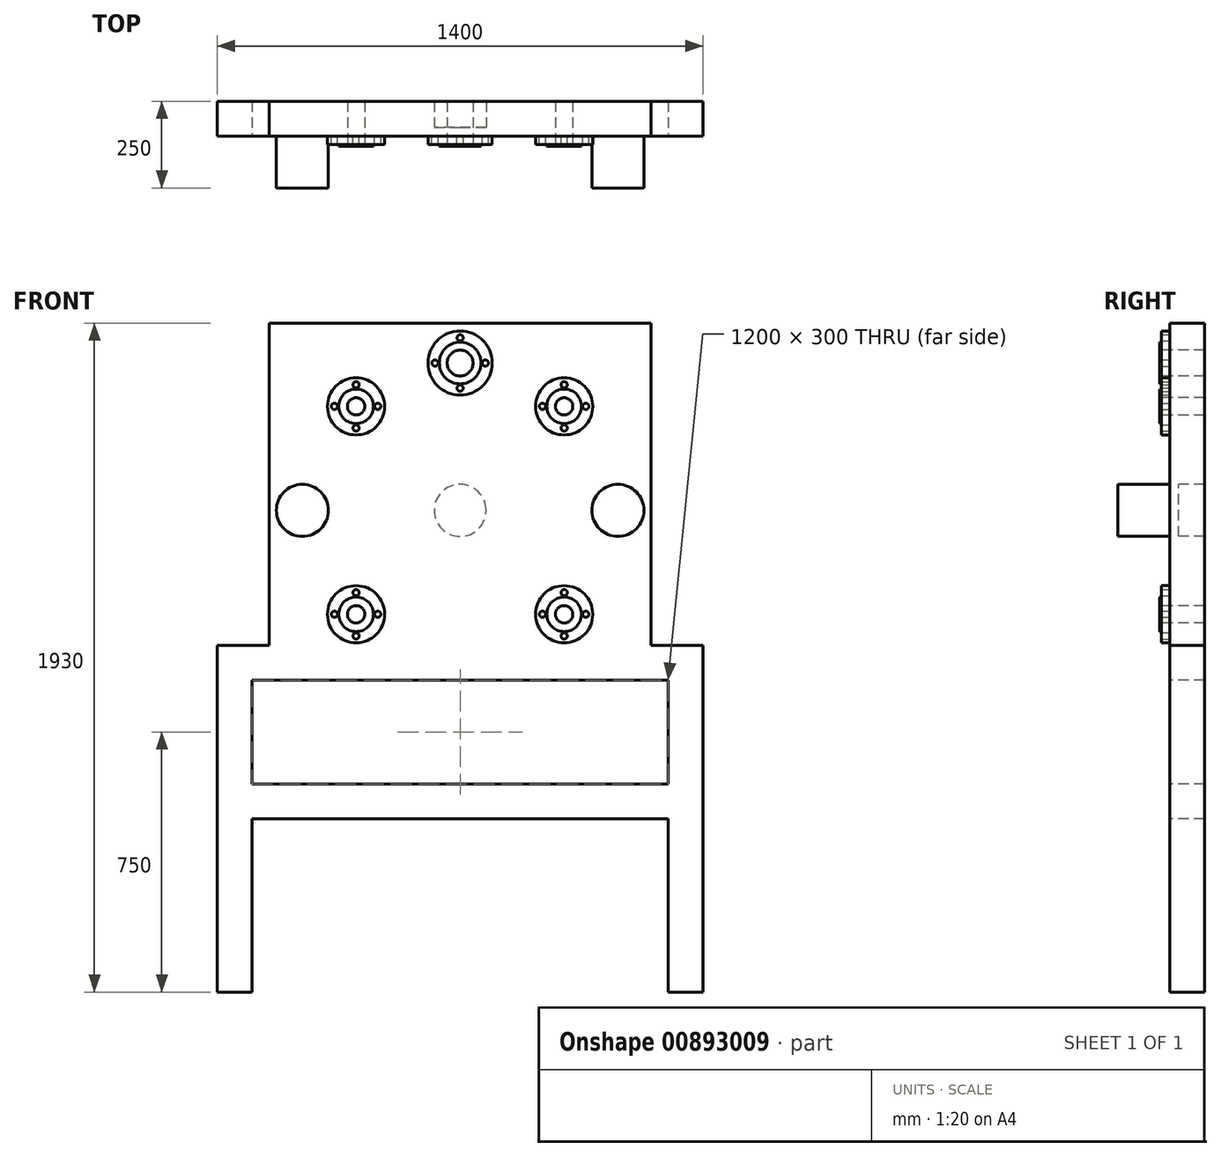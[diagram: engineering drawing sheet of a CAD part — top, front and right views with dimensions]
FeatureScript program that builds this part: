
annotation { "Feature Type Name" : "Feature", "Feature Type Description" : "" }
export const myFeature = defineFeature(function(context is Context, id is Id, definition is map)
    precondition{}
    {
        {
            var Q0;
            Q0=qCreatedBy(makeId("Front.planeOp"),FACE);
            var sketch = newSketch(context, id + "F0", { "sketchPlane" : qUnion([Q0])});
            skLineSegment(sketch, "E0.bottom", {"start": v(550, -965) * mm, "end": v(400, -965) * mm});
            skLineSegment(sketch, "E0.top", {"start": v(550, 965) * mm, "end": v(-550, 965) * mm});
            skLineSegment(sketch, "E0.left", {"start": v(550, -965) * mm, "end": v(550, 965) * mm});
            skLineSegment(sketch, "E0.right", {"start": v(-550, -965) * mm, "end": v(-550, 965) * mm});
            skPoint(sketch, "E0.middle", {"position": v(0, 0) * mm});
            skLineSegment(sketch, "E1.top", {"start": v(-400, -765) * mm, "end": v(400, -765) * mm});
            skLineSegment(sketch, "E1.left", {"start": v(-400, -965) * mm, "end": v(-400, -765) * mm});
            skLineSegment(sketch, "E1.right", {"start": v(400, -965) * mm, "end": v(400, -765) * mm});
            skLineSegment(sketch, "E2.bottom", {"start": v(-400, -615) * mm, "end": v(400, -615) * mm});
            skLineSegment(sketch, "E2.top", {"start": v(-400, -315) * mm, "end": v(400, -315) * mm});
            skLineSegment(sketch, "E2.left", {"start": v(-400, -615) * mm, "end": v(-400, -315) * mm});
            skLineSegment(sketch, "E2.right", {"start": v(400, -615) * mm, "end": v(400, -315) * mm});
            skLineSegment(sketch, "E3.trimOffspring", {"start": v(-400, -965) * mm, "end": v(-550, -965) * mm});
            skLineSegment(sketch, "E4.bottom", {"start": v(-400, -165) * mm, "end": v(400, -165) * mm});
            skLineSegment(sketch, "E4.top", {"start": v(-400, 35) * mm, "end": v(400, 35) * mm});
            skLineSegment(sketch, "E4.left", {"start": v(-400, -165) * mm, "end": v(-400, 35) * mm});
            skLineSegment(sketch, "E4.right", {"start": v(400, -165) * mm, "end": v(400, 35) * mm});
            skPoint(sketch, "E5.middle", {"position": v(0, 425) * mm});
            skSolve(sketch);
        }
        {
            var Q0;
            Q0=makeQuery(id+"F0.imprint","IMPRINT",FACE,{"disambiguationData":[TD([[makeQuery(id+"F0.imprint","IMPRINT",EDGE,{"derivedFrom":sQuery(id+"F0.wireOp",EDGE,"E0.bottom")}),-1.0]])]});
            extrude(context, id + "F1", {"entities" : qUnion([Q0]), "depth" : 100 * mm, "offsetDistance" : 25 * mm});
        }
        {
            var Q0;
            Q0=makeQuery(id+"F1.opExtrude","CAP_FACE",FACE,{"disambiguationData":[OSD([sQuery(id+"F0.wireOp",EDGE,"E0.bottom"),sQuery(id+"F0.wireOp",EDGE,"E0.top"),sQuery(id+"F0.wireOp",EDGE,"E0.left"),sQuery(id+"F0.wireOp",EDGE,"E0.right"),sQuery(id+"F0.wireOp",EDGE,"E1.top"),sQuery(id+"F0.wireOp",EDGE,"E1.left"),sQuery(id+"F0.wireOp",EDGE,"E1.right"),sQuery(id+"F0.wireOp",EDGE,"E2.bottom"),sQuery(id+"F0.wireOp",EDGE,"E2.top"),sQuery(id+"F0.wireOp",EDGE,"E2.left"),sQuery(id+"F0.wireOp",EDGE,"E2.right"),sQuery(id+"F0.wireOp",EDGE,"E3.trimOffspring"),sQuery(id+"F0.wireOp",EDGE,"nSGubIzk-R7de-6MO4-penA-cvBglKJnvsGC"),sQuery(id+"F0.wireOp",EDGE,"E4.bottom"),sQuery(id+"F0.wireOp",EDGE,"E4.top"),sQuery(id+"F0.wireOp",EDGE,"E4.left"),sQuery(id+"F0.wireOp",EDGE,"E4.right")])],"isStart":false});
            var sketch = newSketch(context, id + "F2", { "sketchPlane" : qUnion([Q0])});
            skCircle(sketch, "E6", {"center": v(-300, 125) * mm, "radius": 25 * mm});
            skCircle(sketch, "E7.0", {"center": v(0, 425) * mm, "radius": 75 * mm});
            skCircle(sketch, "E8.0.1.0", {"center": v(-300, 725) * mm, "radius": 25 * mm});
            skCircle(sketch, "E8.1.0.0", {"center": v(300, 125) * mm, "radius": 25 * mm});
            skCircle(sketch, "E8.1.1.0", {"center": v(300, 725) * mm, "radius": 25 * mm});
            skLineSegment(sketch, "E8.direction1", {"start": v(-300, 125) * mm, "end": v(300, 125) * mm, "construction": true});
            skLineSegment(sketch, "E8.direction2", {"start": v(-300, 125) * mm, "end": v(-300, 725) * mm, "construction": true});
            skSolve(sketch);
        }
        {
            var Q0;
            Q0=qSketchRegion(id+"F2",true);
            extrude(context, id + "F3", {"entities" : qUnion([Q0]), "operationType" : NewBodyOperationType.REMOVE, "oppositeDirection" : true, "depth" : 100 * mm, "offsetDistance" : 25 * mm});
        }
        {
            var Q0;
            Q0=makeQuery(id+"F1.opExtrude","CAP_FACE",FACE,{"disambiguationData":[OSD([sQuery(id+"F0.wireOp",EDGE,"E0.bottom"),sQuery(id+"F0.wireOp",EDGE,"E0.top"),sQuery(id+"F0.wireOp",EDGE,"E0.left"),sQuery(id+"F0.wireOp",EDGE,"E0.right"),sQuery(id+"F0.wireOp",EDGE,"E1.top"),sQuery(id+"F0.wireOp",EDGE,"E1.left"),sQuery(id+"F0.wireOp",EDGE,"E1.right"),sQuery(id+"F0.wireOp",EDGE,"E2.bottom"),sQuery(id+"F0.wireOp",EDGE,"E2.top"),sQuery(id+"F0.wireOp",EDGE,"E2.left"),sQuery(id+"F0.wireOp",EDGE,"E2.right"),sQuery(id+"F0.wireOp",EDGE,"E3.trimOffspring"),sQuery(id+"F0.wireOp",EDGE,"nSGubIzk-R7de-6MO4-penA-cvBglKJnvsGC"),sQuery(id+"F0.wireOp",EDGE,"E4.bottom"),sQuery(id+"F0.wireOp",EDGE,"E4.top"),sQuery(id+"F0.wireOp",EDGE,"E4.left"),sQuery(id+"F0.wireOp",EDGE,"E4.right")])],"isStart":false});
            var sketch = newSketch(context, id + "F4", { "sketchPlane" : qUnion([Q0])});
            skCircle(sketch, "E9", {"center": v(-455, 425) * mm, "radius": 75 * mm});
            skCircle(sketch, "E10.MirrorC", {"center": v(455, 425) * mm, "radius": 75 * mm});
            skSolve(sketch);
        }
        {
            var Q0;
            Q0=qSketchRegion(id+"F4",true);
            extrude(context, id + "F5", {"entities" : qUnion([Q0]), "operationType" : NewBodyOperationType.ADD, "depth" : 150 * mm, "offsetDistance" : 25 * mm});
        }
        {
            var Q0;
            Q0=makeQuery(id+"F1.opExtrude","CAP_FACE",FACE,{"disambiguationData":[OSD([sQuery(id+"F0.wireOp",EDGE,"E0.bottom"),sQuery(id+"F0.wireOp",EDGE,"E0.top"),sQuery(id+"F0.wireOp",EDGE,"E0.left"),sQuery(id+"F0.wireOp",EDGE,"E0.right"),sQuery(id+"F0.wireOp",EDGE,"E1.top"),sQuery(id+"F0.wireOp",EDGE,"E1.left"),sQuery(id+"F0.wireOp",EDGE,"E1.right"),sQuery(id+"F0.wireOp",EDGE,"E2.bottom"),sQuery(id+"F0.wireOp",EDGE,"E2.top"),sQuery(id+"F0.wireOp",EDGE,"E2.left"),sQuery(id+"F0.wireOp",EDGE,"E2.right"),sQuery(id+"F0.wireOp",EDGE,"E3.trimOffspring"),sQuery(id+"F0.wireOp",EDGE,"nSGubIzk-R7de-6MO4-penA-cvBglKJnvsGC"),sQuery(id+"F0.wireOp",EDGE,"E4.bottom"),sQuery(id+"F0.wireOp",EDGE,"E4.top"),sQuery(id+"F0.wireOp",EDGE,"E4.left"),sQuery(id+"F0.wireOp",EDGE,"E4.right")])],"isStart":false});
            var sketch = newSketch(context, id + "F6", { "sketchPlane" : qUnion([Q0])});
            skCircle(sketch, "E11", {"center": v(-300, 725) * mm, "radius": 82.5 * mm});
            skCircle(sketch, "E12", {"center": v(-300, 787.5) * mm, "radius": 9 * mm});
            skCircle(sketch, "E13.0", {"center": v(-300, 725) * mm, "radius": 25 * mm});
            skCircle(sketch, "E14.1.0", {"center": v(-362.5, 725) * mm, "radius": 9 * mm});
            skCircle(sketch, "E14.2.0", {"center": v(-300, 662.5) * mm, "radius": 9 * mm});
            skCircle(sketch, "E14.3.0", {"center": v(-237.5, 725) * mm, "radius": 9 * mm});
            skPoint(sketch, "E15.0.1.0", {"position": v(-300, 125) * mm});
            skCircle(sketch, "E15.0.1.1", {"center": v(-300, 125) * mm, "radius": 82.5 * mm});
            skCircle(sketch, "E15.0.1.2", {"center": v(-300, 125) * mm, "radius": 25 * mm});
            skCircle(sketch, "E15.0.1.3", {"center": v(-237.5, 125) * mm, "radius": 9 * mm});
            skCircle(sketch, "E15.0.1.4", {"center": v(-362.5, 125) * mm, "radius": 9 * mm});
            skCircle(sketch, "E15.0.1.5", {"center": v(-300, 187.5) * mm, "radius": 9 * mm});
            skCircle(sketch, "E15.0.1.6", {"center": v(-300, 62.5) * mm, "radius": 9 * mm});
            skPoint(sketch, "E15.1.0.0", {"position": v(300, 725) * mm});
            skCircle(sketch, "E15.1.0.1", {"center": v(300, 725) * mm, "radius": 82.5 * mm});
            skCircle(sketch, "E15.1.0.2", {"center": v(300, 725) * mm, "radius": 25 * mm});
            skCircle(sketch, "E15.1.0.3", {"center": v(362.5, 725) * mm, "radius": 9 * mm});
            skCircle(sketch, "E15.1.0.4", {"center": v(237.5, 725) * mm, "radius": 9 * mm});
            skCircle(sketch, "E15.1.0.5", {"center": v(300, 787.5) * mm, "radius": 9 * mm});
            skCircle(sketch, "E15.1.0.6", {"center": v(300, 662.5) * mm, "radius": 9 * mm});
            skPoint(sketch, "E15.1.1.0", {"position": v(300, 125) * mm});
            skCircle(sketch, "E15.1.1.1", {"center": v(300, 125) * mm, "radius": 82.5 * mm});
            skCircle(sketch, "E15.1.1.2", {"center": v(300, 125) * mm, "radius": 25 * mm});
            skCircle(sketch, "E15.1.1.3", {"center": v(362.5, 125) * mm, "radius": 9 * mm});
            skCircle(sketch, "E15.1.1.4", {"center": v(237.5, 125) * mm, "radius": 9 * mm});
            skCircle(sketch, "E15.1.1.5", {"center": v(300, 187.5) * mm, "radius": 9 * mm});
            skCircle(sketch, "E15.1.1.6", {"center": v(300, 62.5) * mm, "radius": 9 * mm});
            skLineSegment(sketch, "E15.direction1", {"start": v(-300, 662.5) * mm, "end": v(300, 662.5) * mm, "construction": true});
            skLineSegment(sketch, "E15.direction2", {"start": v(-300, 662.5) * mm, "end": v(-300, 62.5) * mm, "construction": true});
            skSolve(sketch);
        }
        {
            var Q0;
            Q0=qSketchRegion(id+"F6",true);
            extrude(context, id + "F7", {"entities" : qUnion([Q0]), "operationType" : NewBodyOperationType.ADD, "depth" : 25 * mm, "offsetDistance" : 25 * mm});
        }
        {
            var Q0;
            Q0=makeQuery(id+"F7.opExtrude","CAP_FACE",FACE,{"disambiguationData":[OSD([sQuery(id+"F6.wireOp",EDGE,"E11"),sQuery(id+"F6.wireOp",EDGE,"E12"),sQuery(id+"F6.wireOp",EDGE,"E13.0"),sQuery(id+"F6.wireOp",EDGE,"E14.1.0"),sQuery(id+"F6.wireOp",EDGE,"E14.2.0"),sQuery(id+"F6.wireOp",EDGE,"E14.3.0")])],"isStart":false});
            var sketch = newSketch(context, id + "F8", { "sketchPlane" : qUnion([Q0])});
            skCircle(sketch, "E16", {"center": v(-300, 725) * mm, "radius": 50 * mm});
            skCircle(sketch, "E17.0.1.0", {"center": v(-300, 125) * mm, "radius": 50 * mm});
            skCircle(sketch, "E17.1.0.0", {"center": v(300, 725) * mm, "radius": 50 * mm});
            skCircle(sketch, "E17.1.1.0", {"center": v(300, 125) * mm, "radius": 50 * mm});
            skLineSegment(sketch, "E17.direction1", {"start": v(-300, 725) * mm, "end": v(300, 725) * mm, "construction": true});
            skLineSegment(sketch, "E17.direction2", {"start": v(-300, 725) * mm, "end": v(-300, 125) * mm, "construction": true});
            skCircle(sketch, "E18", {"center": v(300, 725) * mm, "radius": 25 * mm});
            skCircle(sketch, "E19", {"center": v(300, 125) * mm, "radius": 25 * mm});
            skCircle(sketch, "E20", {"center": v(-300, 125) * mm, "radius": 25 * mm});
            skCircle(sketch, "E21", {"center": v(-300, 725) * mm, "radius": 25 * mm});
            skSolve(sketch);
        }
        {
            var Q0;
            Q0=qSketchRegion(id+"F8",true);
            extrude(context, id + "F9", {"entities" : qUnion([Q0]), "operationType" : NewBodyOperationType.ADD, "depth" : 5 * mm, "offsetDistance" : 25 * mm});
        }
        {
            var Q0;
            {var subQ0=sQuery(id+"F0.wireOp",EDGE,"E4.right");var subQ1=sQuery(id+"F0.wireOp",EDGE,"E4.left");var subQ2=sQuery(id+"F0.wireOp",EDGE,"E4.top");var subQ3=sQuery(id+"F0.wireOp",EDGE,"E1.left");var subQ4=sQuery(id+"F0.wireOp",EDGE,"E4.bottom");var subQ5=sQuery(id+"F0.wireOp",EDGE,"E3.trimOffspring");var subQ6=sQuery(id+"F0.wireOp",EDGE,"E2.right");var subQ7=sQuery(id+"F0.wireOp",EDGE,"E0.left");var subQ8=sQuery(id+"F0.wireOp",EDGE,"E0.top");var subQ9=sQuery(id+"F0.wireOp",EDGE,"E0.right");var subQ10=sQuery(id+"F0.wireOp",EDGE,"E2.bottom");var subQ11=sQuery(id+"F0.wireOp",EDGE,"E0.bottom");var subQ12=sQuery(id+"F0.wireOp",EDGE,"E2.left");var subQ13=sQuery(id+"F0.wireOp",EDGE,"E1.top");var subQ14=sQuery(id+"F0.wireOp",EDGE,"E1.right");var subQ15=sQuery(id+"F0.wireOp",EDGE,"E2.top");Q0=makeQuery(id+"F7.boolean.opBoolean","SPLIT",FACE,{"disambiguationData":[TD([makeQuery(id+"F1.opExtrude","SWEPT_FACE",FACE,{"disambiguationData":[OSD([subQ11])]})])],"derivedFrom":makeQuery(id+"F1.opExtrude","CAP_FACE",FACE,{"disambiguationData":[OSD([subQ11,subQ8,subQ7,subQ9,subQ13,subQ3,subQ14,subQ10,subQ15,subQ12,subQ6,subQ5,subQ4,subQ2,subQ1,subQ0])],"isStart":false})});}
            var sketch = newSketch(context, id + "F10", { "sketchPlane" : qUnion([Q0])});
            skCircle(sketch, "E22.0", {"center": v(0, 425) * mm, "radius": 75 * mm});
            skSolve(sketch);
        }
        {
            var Q0;
            Q0=qSketchRegion(id+"F10",true);
            extrude(context, id + "F11", {"entities" : qUnion([Q0]), "operationType" : NewBodyOperationType.ADD, "oppositeDirection" : true, "depth" : 25 * mm, "offsetDistance" : 25 * mm});
        }
        {
            var Q0;
            {var subQ0=sQuery(id+"F0.wireOp",EDGE,"E4.right");var subQ1=sQuery(id+"F0.wireOp",EDGE,"E4.left");var subQ2=sQuery(id+"F0.wireOp",EDGE,"E4.top");var subQ3=sQuery(id+"F0.wireOp",EDGE,"E1.left");var subQ4=sQuery(id+"F0.wireOp",EDGE,"E4.bottom");var subQ5=sQuery(id+"F0.wireOp",EDGE,"E3.trimOffspring");var subQ6=sQuery(id+"F0.wireOp",EDGE,"E2.right");var subQ7=sQuery(id+"F0.wireOp",EDGE,"E0.left");var subQ8=sQuery(id+"F0.wireOp",EDGE,"E0.top");var subQ9=sQuery(id+"F0.wireOp",EDGE,"E0.right");var subQ10=sQuery(id+"F0.wireOp",EDGE,"E2.bottom");var subQ11=sQuery(id+"F0.wireOp",EDGE,"E0.bottom");var subQ12=sQuery(id+"F0.wireOp",EDGE,"E2.left");var subQ13=sQuery(id+"F0.wireOp",EDGE,"E1.top");var subQ14=sQuery(id+"F0.wireOp",EDGE,"E1.right");var subQ15=sQuery(id+"F0.wireOp",EDGE,"E2.top");Q0=makeQuery(id+"F11.boolean.opBoolean","MERGE",FACE,{"derivedFrom":[makeQuery(id+"F7.boolean.opBoolean","SPLIT",FACE,{"disambiguationData":[TD([makeQuery(id+"F1.opExtrude","SWEPT_FACE",FACE,{"disambiguationData":[OSD([subQ11])]})])],"derivedFrom":makeQuery(id+"F1.opExtrude","CAP_FACE",FACE,{"disambiguationData":[OSD([subQ11,subQ8,subQ7,subQ9,subQ13,subQ3,subQ14,subQ10,subQ15,subQ12,subQ6,subQ5,subQ4,subQ2,subQ1,subQ0])],"isStart":false})}),makeQuery(id+"F11.opExtrude","CAP_FACE",FACE,{"disambiguationData":[OSD([sQuery(id+"F10.wireOp",EDGE,"E22.0")])],"isStart":true})]});}
            var sketch = newSketch(context, id + "F12", { "sketchPlane" : qUnion([Q0])});
            skCircle(sketch, "E23", {"center": v(0, 850) * mm, "radius": 37.5 * mm});
            skPoint(sketch, "E23.centerSnap0", {"position": v(0, 965) * mm});
            skCircle(sketch, "E24.0", {"center": v(300, 725) * mm, "radius": 25 * mm});
            skSolve(sketch);
        }
        {
            var Q0;
            Q0=makeQuery(id+"F12.imprint","IMPRINT",FACE,{"disambiguationData":[TD([[makeQuery(id+"F12.imprint","IMPRINT",EDGE,{"derivedFrom":sQuery(id+"F12.wireOp",EDGE,"E23")}),1.0]])]});
            extrude(context, id + "F13", {"entities" : qUnion([Q0]), "operationType" : NewBodyOperationType.REMOVE, "oppositeDirection" : true, "depth" : 100 * mm, "offsetDistance" : 25 * mm});
        }
        {
            var Q0;
            {var subQ0=sQuery(id+"F0.wireOp",EDGE,"E4.right");var subQ1=sQuery(id+"F0.wireOp",EDGE,"E4.left");var subQ2=sQuery(id+"F0.wireOp",EDGE,"E4.top");var subQ3=sQuery(id+"F0.wireOp",EDGE,"E1.left");var subQ4=sQuery(id+"F0.wireOp",EDGE,"E4.bottom");var subQ5=sQuery(id+"F0.wireOp",EDGE,"E3.trimOffspring");var subQ6=sQuery(id+"F0.wireOp",EDGE,"E2.right");var subQ7=sQuery(id+"F0.wireOp",EDGE,"E0.left");var subQ8=sQuery(id+"F0.wireOp",EDGE,"E0.top");var subQ9=sQuery(id+"F0.wireOp",EDGE,"E0.right");var subQ10=sQuery(id+"F0.wireOp",EDGE,"E2.bottom");var subQ11=sQuery(id+"F0.wireOp",EDGE,"E0.bottom");var subQ12=sQuery(id+"F0.wireOp",EDGE,"E2.left");var subQ13=sQuery(id+"F0.wireOp",EDGE,"E1.top");var subQ14=sQuery(id+"F0.wireOp",EDGE,"E1.right");var subQ15=sQuery(id+"F0.wireOp",EDGE,"E2.top");Q0=makeQuery(id+"F11.boolean.opBoolean","MERGE",FACE,{"derivedFrom":[makeQuery(id+"F7.boolean.opBoolean","SPLIT",FACE,{"disambiguationData":[TD([makeQuery(id+"F1.opExtrude","SWEPT_FACE",FACE,{"disambiguationData":[OSD([subQ11])]})])],"derivedFrom":makeQuery(id+"F1.opExtrude","CAP_FACE",FACE,{"disambiguationData":[OSD([subQ11,subQ8,subQ7,subQ9,subQ13,subQ3,subQ14,subQ10,subQ15,subQ12,subQ6,subQ5,subQ4,subQ2,subQ1,subQ0])],"isStart":false})}),makeQuery(id+"F11.opExtrude","CAP_FACE",FACE,{"disambiguationData":[OSD([sQuery(id+"F10.wireOp",EDGE,"E22.0")])],"isStart":true})]});}
            var sketch = newSketch(context, id + "F14", { "sketchPlane" : qUnion([Q0])});
            skCircle(sketch, "E25", {"center": v(0, 850) * mm, "radius": 92.5 * mm});
            skCircle(sketch, "E26", {"center": v(0, 922.5) * mm, "radius": 9 * mm});
            skCircle(sketch, "E27.1.0", {"center": v(-72.5, 850) * mm, "radius": 9 * mm});
            skCircle(sketch, "E27.2.0", {"center": v(0, 777.5) * mm, "radius": 9 * mm});
            skCircle(sketch, "E27.3.0", {"center": v(72.5, 850) * mm, "radius": 9 * mm});
            skSolve(sketch);
        }
        {
            var Q0;
            Q0=makeQuery(id+"F14.imprint","IMPRINT",FACE,{"disambiguationData":[TD([[makeQuery(id+"F14.imprint","IMPRINT",EDGE,{"derivedFrom":sQuery(id+"F14.wireOp",EDGE,"E25")}),1.0]])]});
            extrude(context, id + "F15", {"entities" : qUnion([Q0]), "operationType" : NewBodyOperationType.ADD, "depth" : 25 * mm, "offsetDistance" : 25 * mm});
        }
        {
            var Q0;
            Q0=makeQuery(id+"F15.opExtrude","CAP_FACE",FACE,{"disambiguationData":[OSD([sQuery(id+"F12.wireOp",EDGE,"E23"),sQuery(id+"F14.wireOp",EDGE,"E25"),sQuery(id+"F14.wireOp",EDGE,"E26"),sQuery(id+"F14.wireOp",EDGE,"E27.1.0"),sQuery(id+"F14.wireOp",EDGE,"E27.2.0"),sQuery(id+"F14.wireOp",EDGE,"E27.3.0")])],"isStart":false});
            var sketch = newSketch(context, id + "F16", { "sketchPlane" : qUnion([Q0])});
            skCircle(sketch, "E28", {"center": v(0, 850) * mm, "radius": 60 * mm});
            skSolve(sketch);
        }
        {
            var Q0;
            Q0=makeQuery(id+"F16.imprint","IMPRINT",FACE,{"disambiguationData":[TD([[makeQuery(id+"F16.imprint","IMPRINT",EDGE,{"derivedFrom":sQuery(id+"F16.wireOp",EDGE,"E28")}),1.0]])]});
            extrude(context, id + "F17", {"entities" : qUnion([Q0]), "operationType" : NewBodyOperationType.ADD, "depth" : 5 * mm, "offsetDistance" : 25 * mm});
        }
        {
            var Q0;
            {var subQ2=sQuery(id+"F0.wireOp",EDGE,"E4.right");var subQ5=sQuery(id+"F0.wireOp",EDGE,"E4.left");var subQ8=sQuery(id+"F0.wireOp",EDGE,"E4.top");var subQ10=sQuery(id+"F0.wireOp",EDGE,"E4.bottom");var subQ12=sQuery(id+"F0.wireOp",EDGE,"E3.trimOffspring");var subQ14=sQuery(id+"F0.wireOp",EDGE,"E2.right");var subQ16=sQuery(id+"F0.wireOp",EDGE,"E0.left");var subQ18=sQuery(id+"F0.wireOp",EDGE,"E0.top");var subQ20=sQuery(id+"F0.wireOp",EDGE,"E0.right");var subQ23=sQuery(id+"F0.wireOp",EDGE,"E2.bottom");var subQ25=sQuery(id+"F0.wireOp",EDGE,"E0.bottom");var subQ26=makeQuery(id+"F1.opExtrude","SWEPT_FACE",FACE,{"disambiguationData":[OSD([subQ25])]});var subQ27=sQuery(id+"F0.wireOp",EDGE,"E2.left");var subQ29=sQuery(id+"F0.wireOp",EDGE,"E1.top");var subQ32=sQuery(id+"F0.wireOp",EDGE,"E1.left");var subQ34=sQuery(id+"F0.wireOp",EDGE,"E1.right");var subQ36=sQuery(id+"F0.wireOp",EDGE,"E2.top");Q0=makeQuery(id+"F15.boolean.opBoolean","SPLIT",FACE,{"disambiguationData":[TD([subQ26])],"derivedFrom":makeQuery(id+"F11.boolean.opBoolean","MERGE",FACE,{"derivedFrom":[makeQuery(id+"F7.boolean.opBoolean","SPLIT",FACE,{"disambiguationData":[TD([subQ26])],"derivedFrom":makeQuery(id+"F1.opExtrude","CAP_FACE",FACE,{"disambiguationData":[OSD([subQ25,subQ18,subQ16,subQ20,subQ29,subQ32,subQ34,subQ23,subQ36,subQ27,subQ14,subQ12,subQ10,subQ8,subQ5,subQ2])],"isStart":false})}),makeQuery(id+"F11.opExtrude","CAP_FACE",FACE,{"disambiguationData":[OSD([sQuery(id+"F10.wireOp",EDGE,"E22.0")])],"isStart":true})]})});}
            var sketch = newSketch(context, id + "F18", { "sketchPlane" : qUnion([Q0])});
            skLineSegment(sketch, "E29.bottom", {"start": v(-568.84, 35) * mm, "end": v(631.16, 35) * mm});
            skLineSegment(sketch, "E29.top", {"start": v(-568.84, -965) * mm, "end": v(631.16, -965) * mm});
            skLineSegment(sketch, "E29.left", {"start": v(-568.84, 35) * mm, "end": v(-568.84, -965) * mm});
            skLineSegment(sketch, "E29.right", {"start": v(631.16, 35) * mm, "end": v(631.16, -965) * mm});
            skSolve(sketch);
        }
        {
            var Q0;
            Q0=qSketchRegion(id+"F18",true);
            extrude(context, id + "F19", {"entities" : qUnion([Q0]), "operationType" : NewBodyOperationType.REMOVE, "oppositeDirection" : true, "depth" : 100 * mm, "offsetDistance" : 25 * mm});
        }
        {
            var Q0;
            Q0=makeQuery(id+"F19.boolean.opBoolean","MERGE",FACE,{"derivedFrom":[makeQuery(id+"F1.opExtrude","SWEPT_FACE",FACE,{"disambiguationData":[OSD([sQuery(id+"F0.wireOp",EDGE,"E4.top")])]}),makeQuery(id+"F19.opExtrude","SWEPT_FACE",FACE,{"disambiguationData":[OSD([sQuery(id+"F18.wireOp",EDGE,"E29.bottom")])]})]});
            var sketch = newSketch(context, id + "F20", { "sketchPlane" : qUnion([Q0])});
            skLineSegment(sketch, "E30.bottom", {"start": v(-700, 0) * mm, "end": v(700, 0) * mm});
            skLineSegment(sketch, "E30.top", {"start": v(-700, 100) * mm, "end": v(700, 100) * mm});
            skLineSegment(sketch, "E30.left", {"start": v(-700, 0) * mm, "end": v(-700, 100) * mm});
            skLineSegment(sketch, "E30.right", {"start": v(700, 0) * mm, "end": v(700, 100) * mm});
            skSolve(sketch);
        }
        {
            var Q0;
            Q0=qSketchRegion(id+"F20",true);
            extrude(context, id + "F21", {"entities" : qUnion([Q0]), "operationType" : NewBodyOperationType.ADD, "depth" : 100 * mm, "offsetDistance" : 25 * mm});
        }
        {
            var Q0;
            {var subQ2=sQuery(id+"F0.wireOp",EDGE,"E4.right");var subQ5=sQuery(id+"F0.wireOp",EDGE,"E4.left");var subQ8=sQuery(id+"F0.wireOp",EDGE,"E4.top");var subQ10=sQuery(id+"F0.wireOp",EDGE,"E4.bottom");var subQ12=sQuery(id+"F0.wireOp",EDGE,"E3.trimOffspring");var subQ14=sQuery(id+"F0.wireOp",EDGE,"E2.right");var subQ16=sQuery(id+"F0.wireOp",EDGE,"E0.left");var subQ18=sQuery(id+"F0.wireOp",EDGE,"E0.top");var subQ20=sQuery(id+"F0.wireOp",EDGE,"E0.right");var subQ23=sQuery(id+"F0.wireOp",EDGE,"E2.bottom");var subQ25=sQuery(id+"F0.wireOp",EDGE,"E0.bottom");var subQ26=makeQuery(id+"F1.opExtrude","SWEPT_FACE",FACE,{"disambiguationData":[OSD([subQ25])]});var subQ27=sQuery(id+"F0.wireOp",EDGE,"E2.left");var subQ29=sQuery(id+"F0.wireOp",EDGE,"E1.top");var subQ32=sQuery(id+"F0.wireOp",EDGE,"E1.left");var subQ34=sQuery(id+"F0.wireOp",EDGE,"E1.right");var subQ36=sQuery(id+"F0.wireOp",EDGE,"E2.top");Q0=makeQuery(id+"F21.boolean.opBoolean","MERGE",FACE,{"derivedFrom":[makeQuery(id+"F15.boolean.opBoolean","SPLIT",FACE,{"disambiguationData":[TD([subQ26])],"derivedFrom":makeQuery(id+"F11.boolean.opBoolean","MERGE",FACE,{"derivedFrom":[makeQuery(id+"F7.boolean.opBoolean","SPLIT",FACE,{"disambiguationData":[TD([subQ26])],"derivedFrom":makeQuery(id+"F1.opExtrude","CAP_FACE",FACE,{"disambiguationData":[OSD([subQ25,subQ18,subQ16,subQ20,subQ29,subQ32,subQ34,subQ23,subQ36,subQ27,subQ14,subQ12,subQ10,subQ8,subQ5,subQ2])],"isStart":false})}),makeQuery(id+"F11.opExtrude","CAP_FACE",FACE,{"disambiguationData":[OSD([sQuery(id+"F10.wireOp",EDGE,"E22.0")])],"isStart":true})]})}),makeQuery(id+"F21.opExtrude","SWEPT_FACE",FACE,{"disambiguationData":[OSD([sQuery(id+"F20.wireOp",EDGE,"E30.top")])]})]});}
            var sketch = newSketch(context, id + "F22", { "sketchPlane" : qUnion([Q0])});
            skLineSegment(sketch, "E31.bottom", {"start": v(-700, -65) * mm, "end": v(-600, -65) * mm});
            skLineSegment(sketch, "E31.top", {"start": v(-700, -965) * mm, "end": v(-600, -965) * mm});
            skLineSegment(sketch, "E31.left", {"start": v(-700, -65) * mm, "end": v(-700, -965) * mm});
            skLineSegment(sketch, "E31.right", {"start": v(700, -65) * mm, "end": v(700, -965) * mm});
            skLineSegment(sketch, "E32.top", {"start": v(-600, -465) * mm, "end": v(600, -465) * mm});
            skLineSegment(sketch, "E32.left", {"start": v(-600, -965) * mm, "end": v(-600, -465) * mm});
            skLineSegment(sketch, "E32.right", {"start": v(600, -965) * mm, "end": v(600, -465) * mm});
            skLineSegment(sketch, "E33.bottom", {"start": v(-600, -365) * mm, "end": v(600, -365) * mm});
            skLineSegment(sketch, "E33.left", {"start": v(-600, -365) * mm, "end": v(-600, -65) * mm});
            skLineSegment(sketch, "E33.right", {"start": v(600, -365) * mm, "end": v(600, -65) * mm});
            skLineSegment(sketch, "E34.trimOffspring", {"start": v(600, -965) * mm, "end": v(700, -965) * mm});
            skLineSegment(sketch, "E35.trimOffspring", {"start": v(600, -65) * mm, "end": v(700, -65) * mm});
            skSolve(sketch);
        }
        {
            var Q0;
            Q0=makeQuery(id+"F22.imprint","IMPRINT",FACE,{"disambiguationData":[TD([[makeQuery(id+"F22.imprint","IMPRINT",EDGE,{"derivedFrom":sQuery(id+"F22.wireOp",EDGE,"E31.bottom")}),-1.0]])]});
            extrude(context, id + "F23", {"entities" : qUnion([Q0]), "operationType" : NewBodyOperationType.ADD, "oppositeDirection" : true, "depth" : 100 * mm, "offsetDistance" : 25 * mm});
        }
    });
